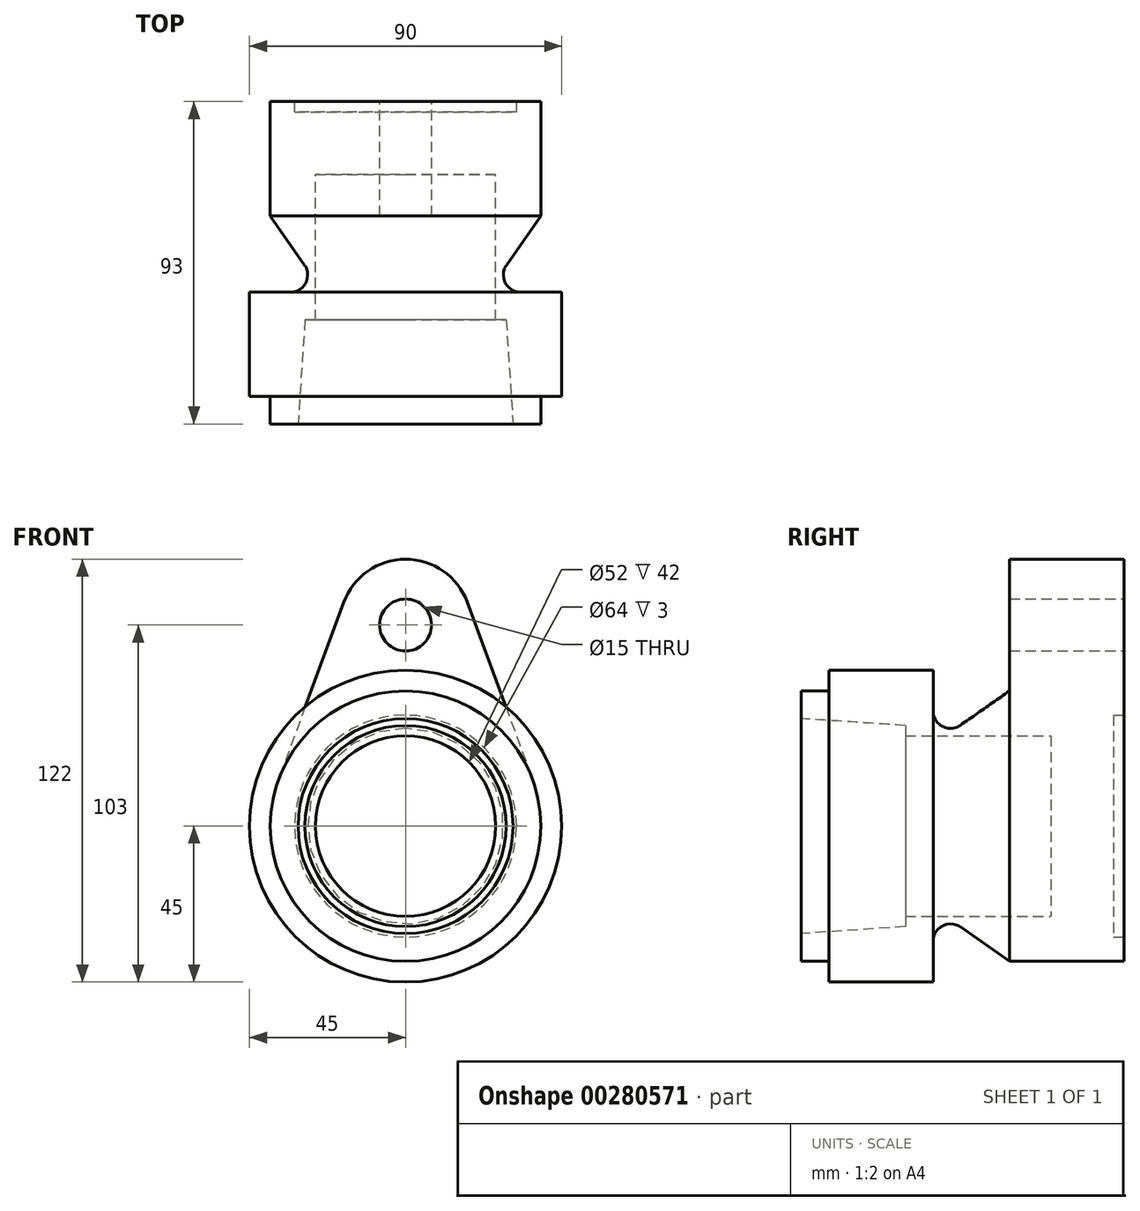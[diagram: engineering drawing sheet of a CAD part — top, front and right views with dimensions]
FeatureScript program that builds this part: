
annotation { "Feature Type Name" : "Feature", "Feature Type Description" : "" }
export const myFeature = defineFeature(function(context is Context, id is Id, definition is map)
    precondition{}
    {
        {
            var Q0;
            Q0=qCreatedBy(makeId("Right.planeOp"),FACE);
            var sketch = newSketch(context, id + "F0", { "sketchPlane" : qUnion([Q0])});
            skLineSegment(sketch, "E0", {"start": v(0, 31) * mm, "end": v(0, 39) * mm});
            skLineSegment(sketch, "E1", {"start": v(0, 39) * mm, "end": v(8, 39) * mm});
            skLineSegment(sketch, "E2", {"start": v(8, 39) * mm, "end": v(8, 45) * mm});
            skLineSegment(sketch, "E3", {"start": v(8, 45) * mm, "end": v(38, 45) * mm});
            skLineSegment(sketch, "E4", {"start": v(38, 45) * mm, "end": v(38, 33.2) * mm});
            skLineSegment(sketch, "E5", {"start": v(45.87, 29.1) * mm, "end": v(60, 39) * mm});
            skLineSegment(sketch, "E6", {"start": v(60, 39) * mm, "end": v(93, 39) * mm});
            skLineSegment(sketch, "E7", {"start": v(93, 39) * mm, "end": v(93, 32) * mm});
            skLineSegment(sketch, "E8", {"start": v(93, 32) * mm, "end": v(90, 32) * mm});
            skLineSegment(sketch, "E9", {"start": v(90, 32) * mm, "end": v(90, 0) * mm});
            skLineSegment(sketch, "E10", {"start": v(90, 0) * mm, "end": v(72, 0) * mm});
            skLineSegment(sketch, "E11", {"start": v(72, 0) * mm, "end": v(72, 26) * mm});
            skLineSegment(sketch, "E12", {"start": v(72, 26) * mm, "end": v(30, 26) * mm});
            skLineSegment(sketch, "E13", {"start": v(30, 26) * mm, "end": v(30, 29) * mm});
            skLineSegment(sketch, "E14", {"start": v(30, 29) * mm, "end": v(0, 31) * mm});
            skPoint(sketch, "E15.visualSharp", {"position": v(38, 23.6) * mm});
            skArc(sketch, "E15.filletArc", {"start": v(38, 33.2) * mm, "mid": v(40.7, 28.77) * mm, "end": v(45.87, 29.1) * mm});
            skSolve(sketch);
        }
        {
            var Q0;
            Q0=makeQuery(id+"F0.imprint","IMPRINT",FACE,{"disambiguationData":[TD([[makeQuery(id+"F0.imprint","IMPRINT",EDGE,{"derivedFrom":sQuery(id+"F0.wireOp",EDGE,"E0")}),-1.0]])]});
            var Q1;
            Q1=sQuery(id+"F0.wireOp",EDGE,"E10");
            revolve(context, id + "F1", {"entities" : qUnion([Q0]), "axis" : qUnion([Q1]), "revolveType" : RevolveType.FULL});
        }
        {
            var Q0;
            Q0=makeQuery(id+"F1.opRevolve","SWEPT_FACE",FACE,{"disambiguationData":[OSD([sQuery(id+"F0.wireOp",EDGE,"E7")])]});
            var sketch = newSketch(context, id + "F2", { "sketchPlane" : qUnion([Q0])});
            skLineSegment(sketch, "E16", {"start": v(0, 0) * mm, "end": v(0, 62.54) * mm, "construction": true});
            skLineSegment(sketch, "E17", {"start": v(12.7, 58) * mm, "end": v(-12.7, 58) * mm, "construction": true});
            skCircle(sketch, "E18", {"center": v(0, 58) * mm, "radius": 7.5 * mm});
            skArc(sketch, "E19", {"start": v(17.83, 64.55) * mm, "mid": v(0, 77) * mm, "end": v(-17.83, 64.55) * mm});
            skLineSegment(sketch, "E20", {"start": v(17.83, 64.55) * mm, "end": v(36.6, 13.45) * mm});
            skLineSegment(sketch, "E21", {"start": v(-17.83, 64.55) * mm, "end": v(-36.6, 13.45) * mm});
            skArc(sketch, "E22", {"start": v(36.6, 13.45) * mm, "mid": v(0, 39) * mm, "end": v(-36.6, 13.45) * mm});
            skLineSegment(sketch, "E23.MirrorC", {"start": v(0, 39) * mm, "end": v(0, 39) * mm});
            skArc(sketch, "E24.MirrorC", {"start": v(-17.83, 64.55) * mm, "mid": v(0, 77) * mm, "end": v(17.83, 64.55) * mm});
            skArc(sketch, "E25.MirrorCS", {"start": v(17.83, -64.55) * mm, "mid": v(0, -77) * mm, "end": v(-17.83, -64.55) * mm});
            skLineSegment(sketch, "E26.MirrorCS", {"start": v(17.83, -64.55) * mm, "end": v(36.6, -13.45) * mm});
            skCircle(sketch, "E27.MirrorC", {"center": v(0, -58) * mm, "radius": 7.5 * mm});
            skLineSegment(sketch, "E28.MirrorCS", {"start": v(-17.83, -64.55) * mm, "end": v(-36.6, -13.45) * mm});
            skLineSegment(sketch, "E29.MirrorCS", {"start": v(12.7, -58) * mm, "end": v(-12.7, -58) * mm, "construction": true});
            skLineSegment(sketch, "E30.MirrorCS", {"start": v(0, 0) * mm, "end": v(0, -62.54) * mm, "construction": true});
            skArc(sketch, "E31.MirrorCS", {"start": v(36.6, -13.45) * mm, "mid": v(0, -39) * mm, "end": v(-36.6, -13.45) * mm});
            skSolve(sketch);
        }
        {
            var Q0;
            Q0=makeQuery(id+"F2.imprint","IMPRINT",FACE,{"disambiguationData":[TD([[makeQuery(id+"F2.imprint","IMPRINT",EDGE,{"derivedFrom":sQuery(id+"F2.wireOp",EDGE,"E22")}),-1.0]])]});
            var Q1;
            Q1=makeQuery(id+"F2.imprint","IMPRINT",FACE,{"disambiguationData":[TD([[makeQuery(id+"F2.imprint","IMPRINT",EDGE,{"derivedFrom":sQuery(id+"F2.wireOp",EDGE,"E25.MirrorCS")}),-1.0]])]});
            extrude(context, id + "F3", {"entities" : qUnion([Q0, Q1]), "operationType" : NewBodyOperationType.ADD, "oppositeDirection" : true, "depth" : 33 * mm});
        }
    });
